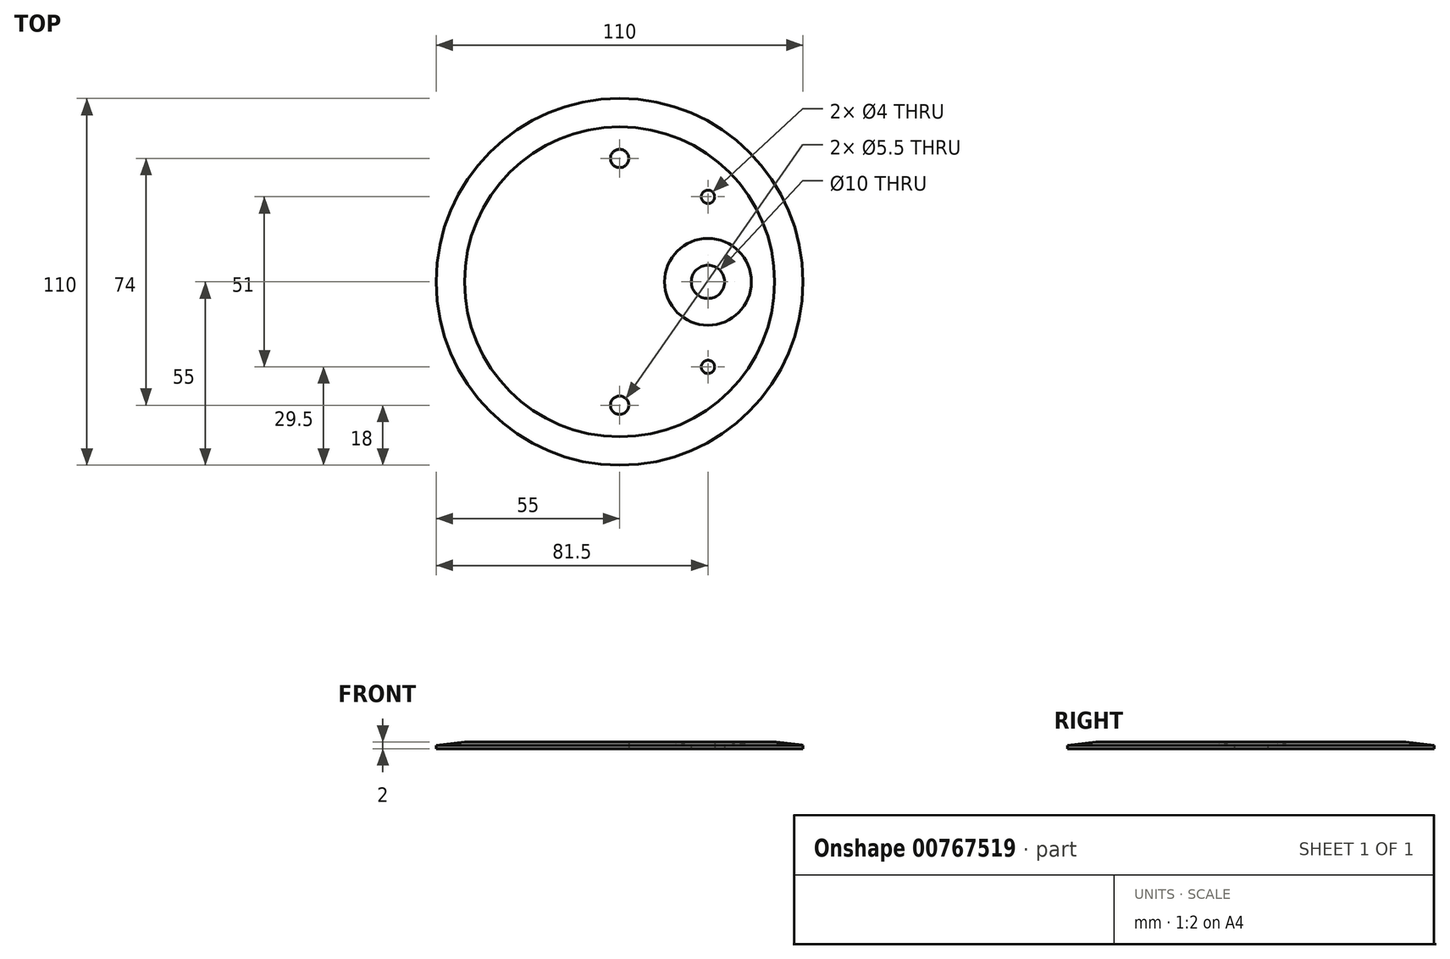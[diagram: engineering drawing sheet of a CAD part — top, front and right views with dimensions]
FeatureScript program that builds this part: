
annotation { "Feature Type Name" : "Feature", "Feature Type Description" : "" }
export const myFeature = defineFeature(function(context is Context, id is Id, definition is map)
    precondition{}
    {
        {
            var Q0;
            Q0=qCreatedBy(makeId("Top.planeOp"),FACE);
            var sketch = newSketch(context, id + "F0", { "sketchPlane" : qUnion([Q0])});
            skCircle(sketch, "E0", {"center": v(0, 0) * mm, "radius": 55 * mm});
            skCircle(sketch, "E1", {"center": v(26.5, 0) * mm, "radius": 5 * mm});
            skPoint(sketch, "E2", {"position": v(55, 0) * mm});
            skCircle(sketch, "E3", {"center": v(26.5, 25.5) * mm, "radius": 2 * mm});
            skCircle(sketch, "E4.1.0", {"center": v(26.5, -25.5) * mm, "radius": 2 * mm});
            skCircle(sketch, "E5", {"center": v(0, 37) * mm, "radius": 2.75 * mm});
            skCircle(sketch, "E6.1.0", {"center": v(0, -37) * mm, "radius": 2.75 * mm});
            skSolve(sketch);
        }
        {
            var Q0;
            Q0=makeQuery(id+"F0.imprint","IMPRINT",FACE,{"disambiguationData":[TD([[makeQuery(id+"F0.imprint","IMPRINT",EDGE,{"derivedFrom":sQuery(id+"F0.wireOp",EDGE,"E0")}),1.0]])]});
            extrude(context, id + "F1", {"entities" : qUnion([Q0]), "depth" : 2 * mm, "offsetDistance" : 25 * mm});
        }
        {
            var Q0;
            Q0=makeQuery(id+"F1.opExtrude","CAP_EDGE",EDGE,{"disambiguationData":[OSD([sQuery(id+"F0.wireOp",EDGE,"E0")])],"isStart":false});
            chamfer(context, id + "F2", {"entities" : qUnion([Q0]), "chamferType" : ChamferType.TWO_OFFSETS, "width1" : 8.5 * mm, "oppositeDirection" : false, "width2" : 1 * mm, "tangentPropagation" : true});
        }
        {
            var Q0;
            Q0=makeQuery(id+"F1.opExtrude","CAP_EDGE",EDGE,{"disambiguationData":[OSD([sQuery(id+"F0.wireOp",EDGE,"E1")])],"isStart":false});
            chamfer(context, id + "F3", {"entities" : qUnion([Q0]), "chamferType" : ChamferType.TWO_OFFSETS, "width1" : 1 * mm, "oppositeDirection" : false, "width2" : 8 * mm, "tangentPropagation" : true});
        }
    });
